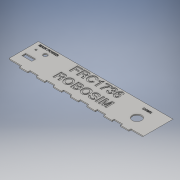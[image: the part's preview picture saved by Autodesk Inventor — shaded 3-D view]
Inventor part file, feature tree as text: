
AUTODESK INVENTOR PART (.ipt)
format: ipt  version: 2016 (Build 200138000, 138)  size: 701,952 bytes
history: native  units: in
note: dims shown in document units (in); Inventor stores cm internally (conversion verified against a paired STEP export)
features: extrude x8, sketch x8, chamfer x1
ambient origin geometry x8: Origin, YZ Plane, XZ Plane, XY Plane, X Axis, Y Axis, Z Axis, Center Point
bodies: Solid1 (feature_tree)
feature tree (17):
  extrude  "Extrusion1"  Depth=3.5in
  extrude  "Extrusion2"  Depth=1.0in
  chamfer  "Chamfer1"  Distance=0.125in
  sketch  "Sketch1"  dims[d0=16.0in d1=3.5in]
  sketch  "Sketch2"  dims[d2=0.125in d3=0.0in d4=2.7559in d6=2.0in d7=0.3937in d9=1.0in d11=0.125in d12=0.0in]
  sketch  "Sketch4"  dims[d19=0.0in d20=0.075in d21=1.1811in d22=0.4528in d24=0.0in d25=0.1969in]
  sketch  "Sketch7"  dims[d38=0.125in d39=0.125in d40=45.0deg]
  sketch  "Sketch8"
  extrude  "Extrusion3"  Depth=0.1969in
  extrude  "Extrusion4"  Depth=0.075in TaperAngle=0.0deg
  extrude  "Extrusion5"  Depth=0.4724in TaperAngle=0.0deg
  extrude  "Extrusion6"  Depth=0.075in TaperAngle=0.0deg
  extrude  "Extrusion7"  [1 undecoded]
  extrude  "Extrusion8"  [1 undecoded]
  sketch  "Sketch3"  dims[d13=1.1in d15=0.0in d16=0.1969in d17=0.1969in]
  sketch  "Sketch5"  dims[d26=0.1969in d27=0.4724in d28=0.1969in d30=0.0in d31=0.1969in]
  sketch  "Sketch6"  dims[d33=0.0in d34=0.075in d36=0.0in d37=0.075in]
note: 2 required parameter values undecoded (feature->parameter linkage not recoverable at this tier; creation-order binding heuristic only, values carry confidence <= 0.55)
